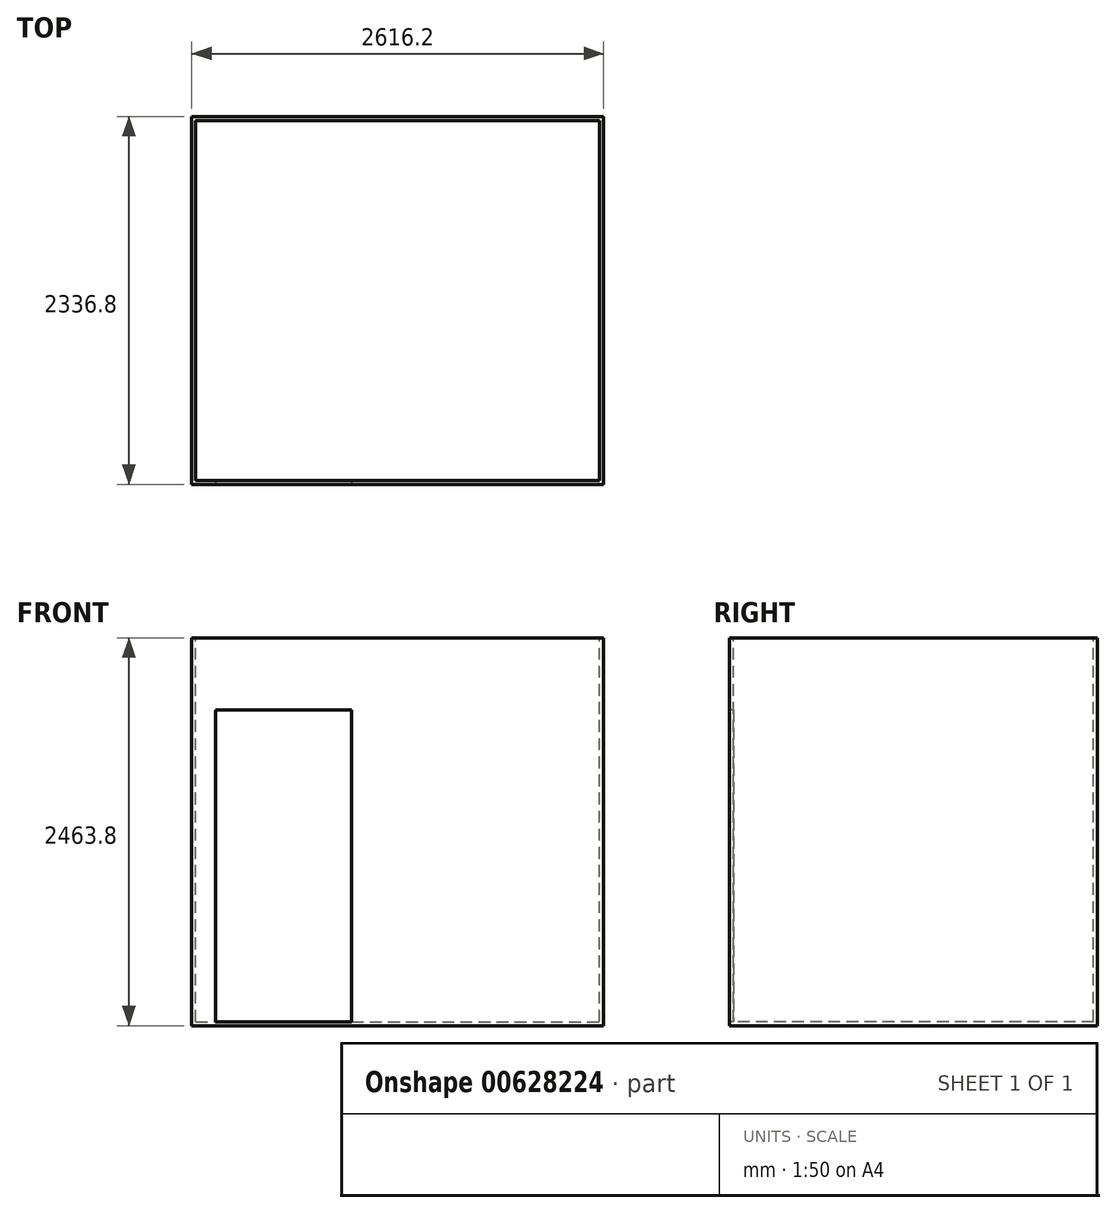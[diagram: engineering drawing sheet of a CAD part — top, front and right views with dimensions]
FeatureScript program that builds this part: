
annotation { "Feature Type Name" : "Feature", "Feature Type Description" : "" }
export const myFeature = defineFeature(function(context is Context, id is Id, definition is map)
    precondition{}
    {
        {
            var Q0;
            Q0=qCreatedBy(makeId("Front.planeOp"),FACE);
            var sketch = newSketch(context, id + "F0", { "sketchPlane" : qUnion([Q0])});
            skLineSegment(sketch, "E0.bottom", {"start": v(0, 0) * mm, "end": v(2616.2, 0) * mm});
            skLineSegment(sketch, "E0.top", {"start": v(0, 2463.8) * mm, "end": v(2616.2, 2463.8) * mm});
            skLineSegment(sketch, "E0.left", {"start": v(0, 0) * mm, "end": v(0, 2463.8) * mm});
            skLineSegment(sketch, "E0.right", {"start": v(2616.2, 0) * mm, "end": v(2616.2, 2463.8) * mm});
            skSolve(sketch);
        }
        {
            var Q0;
            Q0 = qSketchRegion(id + "F0", true);
            extrude(context, id + "F1", {"entities" : qUnion([Q0]), "depth" : 2336.8 * mm, "offsetDistance" : 25.4 * mm});
        }
        {
            var Q0;
            Q0=makeQuery(id+"F1.opExtrude","SWEPT_FACE",FACE,{"disambiguationData":[OSD([sQuery(id+"F0.wireOp",EDGE,"E0.top")])]});
            var sketch = newSketch(context, id + "F2", { "sketchPlane" : qUnion([Q0])});
            skLineSegment(sketch, "E1.bottom", {"start": v(25.4, -25.4) * mm, "end": v(2590.8, -25.4) * mm});
            skLineSegment(sketch, "E1.top", {"start": v(25.4, -2311.4) * mm, "end": v(2590.8, -2311.4) * mm});
            skLineSegment(sketch, "E1.left", {"start": v(25.4, -25.4) * mm, "end": v(25.4, -2311.4) * mm});
            skLineSegment(sketch, "E1.right", {"start": v(2590.8, -25.4) * mm, "end": v(2590.8, -2311.4) * mm});
            skSolve(sketch);
        }
        {
            var Q0;
            Q0 = qSketchRegion(id + "F2", true);
            extrude(context, id + "F3", {"entities" : qUnion([Q0]), "operationType" : NewBodyOperationType.REMOVE, "oppositeDirection" : true, "depth" : 2438.4 * mm, "offsetDistance" : 25.4 * mm});
        }
        {
            var Q0;
            Q0=makeQuery(id+"F1.opExtrude","CAP_FACE",FACE,{"disambiguationData":[OSD([sQuery(id+"F0.wireOp",EDGE,"E0.bottom"),sQuery(id+"F0.wireOp",EDGE,"E0.top"),sQuery(id+"F0.wireOp",EDGE,"E0.left"),sQuery(id+"F0.wireOp",EDGE,"E0.right")])],"isStart":false});
            var sketch = newSketch(context, id + "F4", { "sketchPlane" : qUnion([Q0])});
            skLineSegment(sketch, "E2.bottom", {"start": v(152.4, 2006.6) * mm, "end": v(1016, 2006.6) * mm});
            skLineSegment(sketch, "E2.top", {"start": v(152.4, 25.4) * mm, "end": v(1016, 25.4) * mm});
            skLineSegment(sketch, "E2.left", {"start": v(152.4, 2006.6) * mm, "end": v(152.4, 25.4) * mm});
            skLineSegment(sketch, "E2.right", {"start": v(1016, 2006.6) * mm, "end": v(1016, 25.4) * mm});
            skSolve(sketch);
        }
        {
            var Q0;
            Q0 = qSketchRegion(id + "F4", true);
            extrude(context, id + "F5", {"entities" : qUnion([Q0]), "operationType" : NewBodyOperationType.REMOVE, "oppositeDirection" : true, "depth" : 50.8 * mm, "offsetDistance" : 25.4 * mm});
        }
    });
